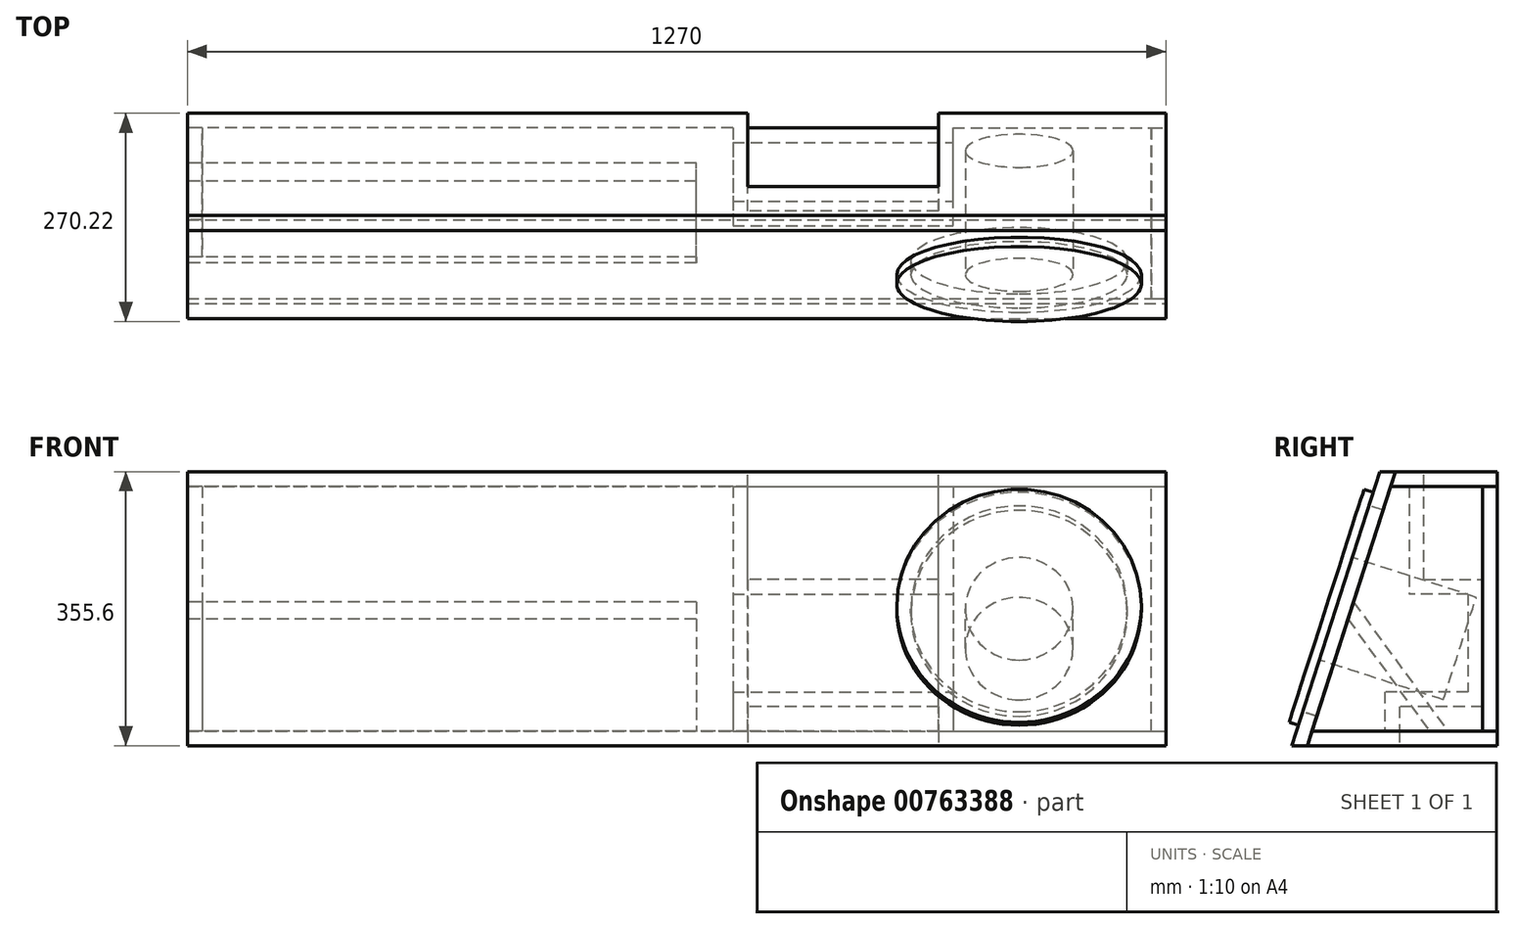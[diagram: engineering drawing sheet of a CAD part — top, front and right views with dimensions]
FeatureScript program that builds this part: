
annotation { "Feature Type Name" : "Feature", "Feature Type Description" : "" }
export const myFeature = defineFeature(function(context is Context, id is Id, definition is map)
    precondition{}
    {
        {
            var Q0;
            Q0=qCreatedBy(makeId("Right.planeOp"),FACE);
            var sketch = newSketch(context, id + "F0", { "sketchPlane" : qUnion([Q0])});
            skLineSegment(sketch, "E0", {"start": v(-46.47, -41.66) * mm, "end": v(220.23, -41.66) * mm});
            skLineSegment(sketch, "E1", {"start": v(220.23, -41.66) * mm, "end": v(220.23, 313.94) * mm});
            skLineSegment(sketch, "E2", {"start": v(220.23, 313.94) * mm, "end": v(67.83, 313.94) * mm});
            skLineSegment(sketch, "E3", {"start": v(67.83, 313.94) * mm, "end": v(-46.47, -41.66) * mm});
            skLineSegment(sketch, "E4.0", {"start": v(220.23, 294.9) * mm, "end": v(81.71, 294.9) * mm});
            skLineSegment(sketch, "E5.0", {"start": v(201.18, -22.6) * mm, "end": v(201.18, 294.9) * mm});
            skLineSegment(sketch, "E6.0", {"start": v(87.84, 313.94) * mm, "end": v(-26.46, -41.66) * mm});
            skLineSegment(sketch, "E7.0", {"start": v(-20.34, -22.6) * mm, "end": v(220.23, -22.6) * mm});
            skSolve(sketch);
        }
        {
            var Q0;
            {var subQ4=sQuery(id+"F0.wireOp",EDGE,"E0");var subQ6=sQuery(id+"F0.wireOp",EDGE,"E1");var subQ7=makeQuery(id+"F0.imprint","INTERSECT",VERTEX,{"derivedFrom":[subQ4,subQ6]});Q0=makeQuery(id+"F0.imprint","IMPRINT",FACE,{"disambiguationData":[TD([[makeQuery(id+"F0.imprint","IMPRINT",EDGE,{"disambiguationData":[TD([[subQ7,1.0]])],"derivedFrom":subQ4}),1.0]])]});}
            extrude(context, id + "F1", {"entities" : qUnion([Q0]), "oppositeDirection" : true, "depth" : 1270 * mm, "offsetDistance" : 25.4 * mm});
        }
        {
            var Q0;
            {var subQ5=sQuery(id+"F0.wireOp",EDGE,"E5.0");Q0=makeQuery(id+"F0.imprint","IMPRINT",FACE,{"disambiguationData":[TD([[makeQuery(id+"F0.imprint","IMPRINT",EDGE,{"derivedFrom":subQ5}),-1.0]])]});}
            extrude(context, id + "F2", {"entities" : qUnion([Q0]), "oppositeDirection" : true, "depth" : 295.27 * mm, "offsetDistance" : 25.4 * mm});
        }
        {
            var Q0;
            Q0=makeQuery(id+"F1.opExtrude","CAP_FACE",FACE,{"disambiguationData":[OSD([sQuery(id+"F0.wireOp",EDGE,"E0"),sQuery(id+"F0.wireOp",EDGE,"E1"),sQuery(id+"F0.wireOp",EDGE,"E6.0"),sQuery(id+"F0.wireOp",EDGE,"E7.0")])],"isStart":false});
            var sketch = newSketch(context, id + "F3", { "sketchPlane" : qUnion([Q0])});
            skPoint(sketch, "E8.0", {"position": v(20.34, -22.6) * mm});
            skPoint(sketch, "E9.0", {"position": v(-81.71, 294.9) * mm});
            skPoint(sketch, "E10.0", {"position": v(-201.18, 294.9) * mm});
            skPoint(sketch, "E11.0", {"position": v(-201.18, -22.6) * mm});
            skPoint(sketch, "E12.0", {"position": v(-220.23, -22.6) * mm});
            skPoint(sketch, "E13.0", {"position": v(-220.23, 294.9) * mm});
            skLineSegment(sketch, "E14", {"start": v(-220.23, 294.9) * mm, "end": v(-201.18, 294.9) * mm});
            skLineSegment(sketch, "E15", {"start": v(-201.18, 294.9) * mm, "end": v(-201.18, -22.6) * mm});
            skLineSegment(sketch, "E16", {"start": v(-201.18, -22.6) * mm, "end": v(-220.23, -22.6) * mm});
            skLineSegment(sketch, "E17", {"start": v(-220.23, -22.6) * mm, "end": v(-220.23, 294.9) * mm});
            skSolve(sketch);
        }
        {
            var Q0;
            Q0 = qSketchRegion(id + "F3", true);
            extrude(context, id + "F4", {"entities" : qUnion([Q0]), "oppositeDirection" : true, "depth" : 727.07 * mm, "offsetDistance" : 25.4 * mm});
        }
        {
            var Q0;
            Q0=makeQuery(id+"F1.opExtrude","SWEPT_FACE",FACE,{"disambiguationData":[OSD([sQuery(id+"F0.wireOp",EDGE,"E7.0")])]});
            var sketch = newSketch(context, id + "F5", { "sketchPlane" : qUnion([Q0])});
            skPoint(sketch, "E18.0", {"position": v(-542.92, 201.18) * mm});
            skPoint(sketch, "E19.0", {"position": v(-295.28, 201.18) * mm});
            skLineSegment(sketch, "E20", {"start": v(-542.92, 201.18) * mm, "end": v(-561.98, 201.18) * mm});
            skLineSegment(sketch, "E21", {"start": v(-561.98, 201.18) * mm, "end": v(-561.98, 74.18) * mm});
            skLineSegment(sketch, "E22", {"start": v(-561.98, 74.18) * mm, "end": v(-276.22, 74.18) * mm});
            skLineSegment(sketch, "E23", {"start": v(-276.22, 74.18) * mm, "end": v(-276.22, 201.18) * mm});
            skLineSegment(sketch, "E24", {"start": v(-276.22, 201.18) * mm, "end": v(-542.92, 201.18) * mm});
            skSolve(sketch);
        }
        {
            var Q0;
            Q0 = qSketchRegion(id + "F5", true);
            extrude(context, id + "F6", {"entities" : qUnion([Q0]), "depth" : 50.8 * mm, "offsetDistance" : 25.4 * mm});
        }
        {
            var Q0;
            Q0=makeQuery(id+"F6.opExtrude","CAP_FACE",FACE,{"disambiguationData":[OSD([sQuery(id+"F5.wireOp",EDGE,"E20"),sQuery(id+"F5.wireOp",EDGE,"E21"),sQuery(id+"F5.wireOp",EDGE,"E22"),sQuery(id+"F5.wireOp",EDGE,"E23"),sQuery(id+"F5.wireOp",EDGE,"E24")])],"isStart":false});
            var sketch = newSketch(context, id + "F7", { "sketchPlane" : qUnion([Q0])});
            skLineSegment(sketch, "E25", {"start": v(-561.98, 201.18) * mm, "end": v(-561.98, 182.13) * mm});
            skLineSegment(sketch, "E26", {"start": v(-561.98, 182.13) * mm, "end": v(-276.22, 182.13) * mm});
            skLineSegment(sketch, "E27", {"start": v(-276.22, 182.13) * mm, "end": v(-276.22, 201.18) * mm});
            skLineSegment(sketch, "E28", {"start": v(-276.22, 201.18) * mm, "end": v(-561.98, 201.18) * mm});
            skSolve(sketch);
        }
        {
            var Q0;
            Q0 = qSketchRegion(id + "F7", true);
            extrude(context, id + "F8", {"entities" : qUnion([Q0]), "operationType" : NewBodyOperationType.ADD, "depth" : 127 * mm, "offsetDistance" : 25.4 * mm});
        }
        {
            var Q0;
            Q0=makeQuery(id+"F8.opExtrude","CAP_FACE",FACE,{"disambiguationData":[OSD([sQuery(id+"F7.wireOp",EDGE,"E25"),sQuery(id+"F7.wireOp",EDGE,"E26"),sQuery(id+"F7.wireOp",EDGE,"E27"),sQuery(id+"F7.wireOp",EDGE,"E28")])],"isStart":false});
            var sketch = newSketch(context, id + "F9", { "sketchPlane" : qUnion([Q0])});
            skLineSegment(sketch, "E29", {"start": v(-561.98, 201.18) * mm, "end": v(-561.98, 105.93) * mm});
            skLineSegment(sketch, "E30", {"start": v(-561.98, 105.93) * mm, "end": v(-276.22, 105.93) * mm});
            skLineSegment(sketch, "E31", {"start": v(-276.22, 105.93) * mm, "end": v(-276.22, 201.18) * mm});
            skLineSegment(sketch, "E32", {"start": v(-276.22, 201.18) * mm, "end": v(-561.98, 201.18) * mm});
            skSolve(sketch);
        }
        {
            var Q0;
            Q0 = qSketchRegion(id + "F9", true);
            extrude(context, id + "F10", {"entities" : qUnion([Q0]), "operationType" : NewBodyOperationType.ADD, "depth" : 139.7 * mm, "offsetDistance" : 25.4 * mm});
        }
        {
            var Q0;
            {var subQ1=sQuery(id+"F0.wireOp",EDGE,"E1");var subQ4=sQuery(id+"F0.wireOp",EDGE,"E2");var subQ5=makeQuery(id+"F0.imprint","INTERSECT",VERTEX,{"derivedFrom":[subQ1,subQ4]});Q0=makeQuery(id+"F0.imprint","IMPRINT",FACE,{"disambiguationData":[TD([[makeQuery(id+"F0.imprint","IMPRINT",EDGE,{"disambiguationData":[TD([[subQ5,1.0]])],"derivedFrom":subQ1}),1.0]])]});}
            extrude(context, id + "F11", {"entities" : qUnion([Q0]), "oppositeDirection" : true, "depth" : 1270 * mm, "offsetDistance" : 25.4 * mm});
        }
        {
            var Q0;
            {var subQ0=sQuery(id+"F0.wireOp",EDGE,"E3");Q0=makeQuery(id+"F0.imprint","IMPRINT",FACE,{"disambiguationData":[TD([[makeQuery(id+"F0.imprint","IMPRINT",EDGE,{"derivedFrom":subQ0}),1.0]])]});}
            extrude(context, id + "F12", {"entities" : qUnion([Q0]), "oppositeDirection" : true, "depth" : 1270 * mm, "offsetDistance" : 25.4 * mm});
        }
        {
            var Q0;
            Q0=makeQuery(id+"F12.opExtrude","SWEPT_FACE",FACE,{"disambiguationData":[OSD([sQuery(id+"F0.wireOp",EDGE,"E3")])]});
            var sketch = newSketch(context, id + "F13", { "sketchPlane" : qUnion([Q0])});
            skLineSegment(sketch, "E33", {"start": v(0, 132.88) * mm, "end": v(-190.5, 132.88) * mm, "construction": true});
            skCircle(sketch, "E34", {"center": v(-190.5, 132.88) * mm, "radius": 140.5 * mm});
            skSolve(sketch);
        }
        {
            var Q0;
            Q0=makeQuery(id+"F13.imprint","IMPRINT",FACE,{"disambiguationData":[TD([[makeQuery(id+"F13.imprint","IMPRINT",EDGE,{"derivedFrom":sQuery(id+"F13.wireOp",EDGE,"E34")}),1.0]])]});
            extrude(context, id + "F14", {"entities" : qUnion([Q0]), "operationType" : NewBodyOperationType.REMOVE, "oppositeDirection" : true, "depth" : 25.4 * mm, "offsetDistance" : 25.4 * mm});
        }
        {
            var Q0;
            Q0=makeQuery(id+"F13.imprint","IMPRINT",FACE,{"disambiguationData":[TD([[makeQuery(id+"F13.imprint","IMPRINT",EDGE,{"derivedFrom":sQuery(id+"F13.wireOp",EDGE,"E34")}),-1.0]])]});
            var sketch = newSketch(context, id + "F15", { "sketchPlane" : qUnion([Q0])});
            skPoint(sketch, "E35.0", {"position": v(-190.5, 132.88) * mm});
            skCircle(sketch, "E36", {"center": v(-190.5, 132.88) * mm, "radius": 69.85 * mm});
            skSolve(sketch);
        }
        {
            var Q0;
            Q0 = qSketchRegion(id + "F15", true);
            extrude(context, id + "F16", {"entities" : qUnion([Q0]), "oppositeDirection" : true, "depth" : 168.9 * mm, "offsetDistance" : 25.4 * mm});
        }
        {
            var Q0;
            Q0=makeQuery(id+"F13.imprint","IMPRINT",FACE,{"disambiguationData":[TD([[makeQuery(id+"F13.imprint","IMPRINT",EDGE,{"derivedFrom":sQuery(id+"F13.wireOp",EDGE,"E34")}),-1.0]])]});
            var sketch = newSketch(context, id + "F17", { "sketchPlane" : qUnion([Q0])});
            skPoint(sketch, "E37.0", {"position": v(-190.5, 132.88) * mm});
            skCircle(sketch, "E38", {"center": v(-190.5, 132.88) * mm, "radius": 158.75 * mm});
            skSolve(sketch);
        }
        {
            var Q0;
            Q0 = qSketchRegion(id + "F17", true);
            extrude(context, id + "F18", {"entities" : qUnion([Q0]), "operationType" : NewBodyOperationType.ADD, "depth" : 12.7 * mm, "offsetDistance" : 25.4 * mm});
        }
        {
            var Q0;
            {var subQ3=sQuery(id+"F0.wireOp",EDGE,"E5.0");Q0=makeQuery(id+"F0.imprint","IMPRINT",FACE,{"disambiguationData":[TD([[makeQuery(id+"F0.imprint","IMPRINT",EDGE,{"derivedFrom":subQ3}),1.0]])]});}
            extrude(context, id + "F19", {"entities" : qUnion([Q0]), "oppositeDirection" : true, "depth" : 19.05 * mm, "offsetDistance" : 25.4 * mm});
        }
        {
            var Q0;
            Q0=makeQuery(id+"F11.opExtrude","CAP_FACE",FACE,{"disambiguationData":[OSD([sQuery(id+"F0.wireOp",EDGE,"E1"),sQuery(id+"F0.wireOp",EDGE,"E2"),sQuery(id+"F0.wireOp",EDGE,"E4.0"),sQuery(id+"F0.wireOp",EDGE,"E6.0")])],"isStart":false});
            var sketch = newSketch(context, id + "F20", { "sketchPlane" : qUnion([Q0])});
            skPoint(sketch, "E39.0", {"position": v(-201.18, 294.9) * mm});
            skPoint(sketch, "E40.0", {"position": v(-81.71, 294.9) * mm});
            skPoint(sketch, "E41.0", {"position": v(20.34, -22.6) * mm});
            skPoint(sketch, "E42.0", {"position": v(-201.18, -22.6) * mm});
            skLineSegment(sketch, "E43", {"start": v(20.34, -22.6) * mm, "end": v(-132.06, -22.6) * mm});
            skLineSegment(sketch, "E44.0", {"start": v(-87.84, 313.94) * mm, "end": v(26.46, -41.66) * mm});
            skLineSegment(sketch, "E45", {"start": v(20.34, -22.6) * mm, "end": v(-26.3, 122.48) * mm});
            skLineSegment(sketch, "E46", {"start": v(-26.3, 122.48) * mm, "end": v(-132.06, -22.6) * mm});
            skLineSegment(sketch, "E47", {"start": v(-132.06, -22.6) * mm, "end": v(-201.18, -22.6) * mm});
            skLineSegment(sketch, "E48", {"start": v(-201.18, 294.9) * mm, "end": v(-201.18, -22.6) * mm});
            skLineSegment(sketch, "E49", {"start": v(-201.18, 294.9) * mm, "end": v(-81.71, 294.9) * mm});
            skLineSegment(sketch, "E50.0", {"start": v(-33.51, 144.92) * mm, "end": v(-155.64, -22.6) * mm});
            skSolve(sketch);
        }
        {
            var Q0;
            {var subQ1=sQuery(id+"F20.wireOp",EDGE,"E48");Q0=makeQuery(id+"F20.imprint","IMPRINT",FACE,{"disambiguationData":[TD([[makeQuery(id+"F20.imprint","IMPRINT",EDGE,{"derivedFrom":subQ1}),1.0]])]});}
            extrude(context, id + "F21", {"entities" : qUnion([Q0]), "oppositeDirection" : true, "depth" : 19.05 * mm, "offsetDistance" : 25.4 * mm});
        }
        {
            var Q0;
            {var subQ0=sQuery(id+"F20.wireOp",EDGE,"E46");Q0=makeQuery(id+"F20.imprint","IMPRINT",FACE,{"disambiguationData":[TD([[makeQuery(id+"F20.imprint","IMPRINT",EDGE,{"derivedFrom":subQ0}),-1.0]])]});}
            extrude(context, id + "F22", {"entities" : qUnion([Q0]), "oppositeDirection" : true, "depth" : 660.4 * mm, "offsetDistance" : 25.4 * mm});
        }
        {
            var Q0;
            Q0=makeQuery(id+"F1.opExtrude","SWEPT_FACE",FACE,{"disambiguationData":[OSD([sQuery(id+"F0.wireOp",EDGE,"E0")])]});
            var sketch = newSketch(context, id + "F23", { "sketchPlane" : qUnion([Q0])});
            skLineSegment(sketch, "E51.0", {"start": v(-561.98, -74.18) * mm, "end": v(-276.22, -74.18) * mm});
            skPoint(sketch, "E52.0", {"position": v(-542.92, -220.23) * mm});
            skPoint(sketch, "E53.0", {"position": v(-295.28, -220.23) * mm});
            skLineSegment(sketch, "E54.0", {"start": v(-561.98, -93.23) * mm, "end": v(-276.22, -93.23) * mm});
            skLineSegment(sketch, "E55", {"start": v(-542.92, -220.23) * mm, "end": v(-542.92, -93.23) * mm});
            skLineSegment(sketch, "E56", {"start": v(-542.92, -220.23) * mm, "end": v(-295.28, -220.23) * mm});
            skLineSegment(sketch, "E57", {"start": v(-295.28, -220.23) * mm, "end": v(-295.28, -93.23) * mm});
            skSolve(sketch);
        }
        {
            var Q0;
            {var subQ0=sQuery(id+"F23.wireOp",EDGE,"E55");Q0=makeQuery(id+"F23.imprint","IMPRINT",FACE,{"disambiguationData":[TD([[makeQuery(id+"F23.imprint","IMPRINT",EDGE,{"derivedFrom":subQ0}),-1.0]])]});}
            extrude(context, id + "F24", {"entities" : qUnion([Q0]), "operationType" : NewBodyOperationType.REMOVE, "oppositeDirection" : true, "depth" : 19.05 * mm, "offsetDistance" : 25.4 * mm});
        }
        {
            var Q0;
            Q0=makeQuery(id+"F6.opExtrude","CAP_FACE",FACE,{"disambiguationData":[OSD([sQuery(id+"F5.wireOp",EDGE,"E20"),sQuery(id+"F5.wireOp",EDGE,"E21"),sQuery(id+"F5.wireOp",EDGE,"E22"),sQuery(id+"F5.wireOp",EDGE,"E23"),sQuery(id+"F5.wireOp",EDGE,"E24")])],"isStart":true});
            var sketch = newSketch(context, id + "F25", { "sketchPlane" : qUnion([Q0])});
            skPoint(sketch, "E58.0", {"position": v(-295.28, -93.23) * mm});
            skPoint(sketch, "E59.0", {"position": v(-542.92, -93.23) * mm});
            skPoint(sketch, "E60.0", {"position": v(-561.98, -182.13) * mm});
            skPoint(sketch, "E61.0", {"position": v(-542.92, -201.18) * mm});
            skPoint(sketch, "E62.0", {"position": v(-295.28, -201.18) * mm});
            skLineSegment(sketch, "E63", {"start": v(-295.28, -201.18) * mm, "end": v(-295.28, -93.23) * mm});
            skLineSegment(sketch, "E64", {"start": v(-295.28, -93.23) * mm, "end": v(-542.92, -93.23) * mm});
            skLineSegment(sketch, "E65", {"start": v(-542.92, -93.23) * mm, "end": v(-542.92, -201.18) * mm});
            skLineSegment(sketch, "E66", {"start": v(-542.92, -201.18) * mm, "end": v(-295.28, -201.18) * mm});
            skSolve(sketch);
        }
        {
            var Q0;
            Q0=makeQuery(id+"F25.imprint","IMPRINT",FACE,{"disambiguationData":[TD([[makeQuery(id+"F25.imprint","IMPRINT",EDGE,{"derivedFrom":sQuery(id+"F25.wireOp",EDGE,"E63")}),1.0]])]});
            extrude(context, id + "F26", {"entities" : qUnion([Q0]), "operationType" : NewBodyOperationType.REMOVE, "oppositeDirection" : true, "depth" : 31.75 * mm, "offsetDistance" : 25.4 * mm});
        }
        {
            var Q0;
            Q0=makeQuery(id+"F11.opExtrude","SWEPT_FACE",FACE,{"disambiguationData":[OSD([sQuery(id+"F0.wireOp",EDGE,"E2")])]});
            var sketch = newSketch(context, id + "F27", { "sketchPlane" : qUnion([Q0])});
            skLineSegment(sketch, "E67.0", {"start": v(-561.98, 105.93) * mm, "end": v(-276.22, 105.93) * mm});
            skPoint(sketch, "E68.0", {"position": v(-295.28, 201.18) * mm});
            skPoint(sketch, "E69.0", {"position": v(-542.92, 201.18) * mm});
            skLineSegment(sketch, "E70.0", {"start": v(-561.98, 124.98) * mm, "end": v(-276.22, 124.98) * mm});
            skLineSegment(sketch, "E71", {"start": v(-295.28, 201.18) * mm, "end": v(-295.28, 124.98) * mm});
            skLineSegment(sketch, "E72", {"start": v(-542.92, 201.18) * mm, "end": v(-542.92, 124.98) * mm});
            skLineSegment(sketch, "E73", {"start": v(-295.28, 201.18) * mm, "end": v(-295.28, 220.23) * mm});
            skLineSegment(sketch, "E74", {"start": v(-295.28, 220.23) * mm, "end": v(-542.92, 220.23) * mm});
            skLineSegment(sketch, "E75", {"start": v(-542.92, 220.23) * mm, "end": v(-542.92, 201.18) * mm});
            skSolve(sketch);
        }
        {
            var Q0;
            Q0 = qSketchRegion(id + "F27", true);
            extrude(context, id + "F28", {"entities" : qUnion([Q0]), "operationType" : NewBodyOperationType.REMOVE, "oppositeDirection" : true, "depth" : 19.05 * mm, "offsetDistance" : 25.4 * mm});
        }
        {
            var Q0;
            Q0=makeQuery(id+"F10.opExtrude","CAP_FACE",FACE,{"disambiguationData":[OSD([sQuery(id+"F9.wireOp",EDGE,"E29"),sQuery(id+"F9.wireOp",EDGE,"E30"),sQuery(id+"F9.wireOp",EDGE,"E31"),sQuery(id+"F9.wireOp",EDGE,"E32")])],"isStart":false});
            var sketch = newSketch(context, id + "F29", { "sketchPlane" : qUnion([Q0])});
            skPoint(sketch, "E76.0", {"position": v(-295.28, 124.98) * mm});
            skPoint(sketch, "E77.0", {"position": v(-295.28, 201.18) * mm});
            skPoint(sketch, "E78.0", {"position": v(-542.92, 201.18) * mm});
            skPoint(sketch, "E79.0", {"position": v(-542.92, 124.98) * mm});
            skLineSegment(sketch, "E80", {"start": v(-542.92, 124.98) * mm, "end": v(-295.28, 124.98) * mm});
            skLineSegment(sketch, "E81", {"start": v(-295.28, 124.98) * mm, "end": v(-295.28, 201.18) * mm});
            skLineSegment(sketch, "E82", {"start": v(-295.28, 201.18) * mm, "end": v(-542.92, 201.18) * mm});
            skLineSegment(sketch, "E83", {"start": v(-542.92, 201.18) * mm, "end": v(-542.92, 124.98) * mm});
            skSolve(sketch);
        }
        {
            var Q0;
            Q0 = qSketchRegion(id + "F29", true);
            extrude(context, id + "F30", {"entities" : qUnion([Q0]), "operationType" : NewBodyOperationType.REMOVE, "oppositeDirection" : true, "depth" : 120.65 * mm, "offsetDistance" : 25.4 * mm});
        }
    });
